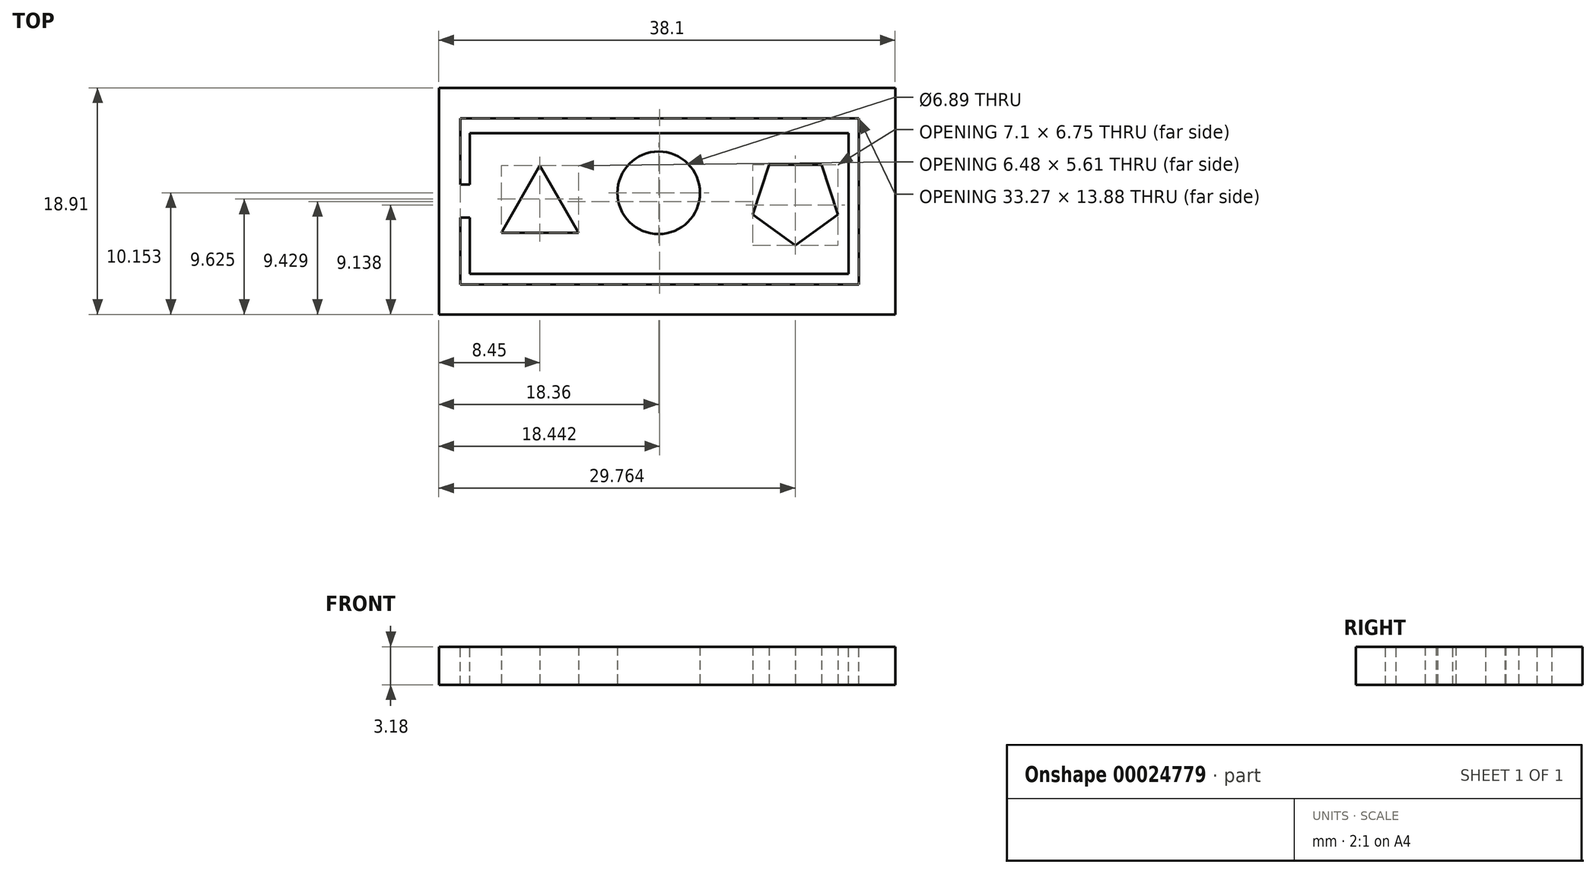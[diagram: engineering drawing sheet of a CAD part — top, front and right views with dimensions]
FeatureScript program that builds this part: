
annotation { "Feature Type Name" : "Feature", "Feature Type Description" : "" }
export const myFeature = defineFeature(function(context is Context, id is Id, definition is map)
    precondition{}
    {
        {
            var Q0;
            Q0=qCreatedBy(makeId("Top.planeOp"),FACE);
            var sketch = newSketch(context, id + "F0", { "sketchPlane" : qUnion([Q0])});
            skLineSegment(sketch, "E0", {"start": v(-18.36, 0) * mm, "end": v(19.74, 0) * mm});
            skLineSegment(sketch, "E1", {"start": v(-18.36, 0) * mm, "end": v(-18.36, 18.9) * mm});
            skLineSegment(sketch, "E2", {"start": v(-18.36, 18.9) * mm, "end": v(19.74, 18.9) * mm});
            skLineSegment(sketch, "E3", {"start": v(19.74, 18.9) * mm, "end": v(19.74, 0) * mm});
            skLineSegment(sketch, "E4", {"start": v(-9.9, 12.43) * mm, "end": v(-13.15, 6.82) * mm});
            skLineSegment(sketch, "E5", {"start": v(-13.15, 6.82) * mm, "end": v(-6.67, 6.82) * mm});
            skLineSegment(sketch, "E6", {"start": v(-6.67, 6.82) * mm, "end": v(-9.9, 12.43) * mm});
            skCircle(sketch, "E7", {"center": v(0, 10.15) * mm, "radius": 3.45 * mm});
            skCircle(sketch, "E8.cCircle", {"center": v(11.4, 9.5) * mm, "radius": 3.73 * mm, "construction": true});
            skLineSegment(sketch, "E8.0", {"start": v(11.4, 5.76) * mm, "end": v(7.86, 8.34) * mm});
            skLineSegment(sketch, "E8.1", {"start": v(7.86, 8.34) * mm, "end": v(9.21, 12.51) * mm});
            skLineSegment(sketch, "E8.2", {"start": v(9.21, 12.51) * mm, "end": v(13.6, 12.51) * mm});
            skLineSegment(sketch, "E8.3", {"start": v(13.6, 12.51) * mm, "end": v(14.95, 8.34) * mm});
            skLineSegment(sketch, "E8.4", {"start": v(14.95, 8.34) * mm, "end": v(11.4, 5.76) * mm});
            skSolve(sketch);
        }
        {
            var Q0;
            {var subQ6=sQuery(id+"F0.wireOp",EDGE,"E0");Q0=makeQuery(id+"F0.imprint","IMPRINT",FACE,{"disambiguationData":[TD([[makeQuery(id+"F0.imprint","IMPRINT",EDGE,{"derivedFrom":subQ6}),1.0]])]});}
            extrude(context, id + "F1", {"entities" : qUnion([Q0]), "depth" : 3.17 * mm});
        }
        {
            var Q0;
            Q0=makeQuery(id+"F1.opExtrude","CAP_FACE",FACE,{"disambiguationData":[OSD([sQuery(id+"F0.wireOp",EDGE,"E0"),sQuery(id+"F0.wireOp",EDGE,"E1"),sQuery(id+"F0.wireOp",EDGE,"E2"),sQuery(id+"F0.wireOp",EDGE,"E3"),sQuery(id+"F0.wireOp",EDGE,"E4"),sQuery(id+"F0.wireOp",EDGE,"E5"),sQuery(id+"F0.wireOp",EDGE,"E6"),sQuery(id+"F0.wireOp",EDGE,"E7"),sQuery(id+"F0.wireOp",EDGE,"E8.0"),sQuery(id+"F0.wireOp",EDGE,"E8.1"),sQuery(id+"F0.wireOp",EDGE,"E8.2"),sQuery(id+"F0.wireOp",EDGE,"E8.3"),sQuery(id+"F0.wireOp",EDGE,"E8.4")])],"isStart":false});
            cPlane(context, id + "F2", {"entities" : qUnion([Q0]), "cplaneType" : CPlaneType.OFFSET, "offset" : 0 * mm, "width" : 152.4 * mm, "height" : 152.4 * mm});
        }
        {
            var Q0;
            Q0=qCreatedBy(id+"F2.planeOp",FACE);
            var sketch = newSketch(context, id + "F3", { "sketchPlane" : qUnion([Q0])});
            skLineSegment(sketch, "E9", {"start": v(-16.55, 8.1) * mm, "end": v(-16.55, 2.49) * mm});
            skLineSegment(sketch, "E10", {"start": v(-16.55, 2.49) * mm, "end": v(16.72, 2.49) * mm});
            skLineSegment(sketch, "E11", {"start": v(16.72, 2.49) * mm, "end": v(16.72, 16.37) * mm});
            skLineSegment(sketch, "E12", {"start": v(16.72, 16.37) * mm, "end": v(-15.77, 16.37) * mm});
            skLineSegment(sketch, "E13", {"start": v(-16.55, 16.37) * mm, "end": v(-16.55, 10.86) * mm});
            skLineSegment(sketch, "E14.bottom", {"start": v(-16.55, 8.1) * mm, "end": v(-15.77, 8.1) * mm});
            skLineSegment(sketch, "E14.right", {"start": v(-15.77, 8.1) * mm, "end": v(-15.77, 3.38) * mm});
            skLineSegment(sketch, "E15.bottom", {"start": v(-15.77, 3.38) * mm, "end": v(15.85, 3.38) * mm});
            skLineSegment(sketch, "E16.right", {"start": v(15.85, 3.38) * mm, "end": v(15.85, 15.13) * mm});
            skLineSegment(sketch, "E17.bottom", {"start": v(15.85, 15.13) * mm, "end": v(-15.77, 15.13) * mm});
            skLineSegment(sketch, "E18.top", {"start": v(-15.77, 10.86) * mm, "end": v(-16.55, 10.86) * mm});
            skLineSegment(sketch, "E18.left", {"start": v(-15.77, 15.13) * mm, "end": v(-15.77, 10.86) * mm});
            skPoint(sketch, "E19.orphan", {"position": v(-15.77, 16.37) * mm});
            skLineSegment(sketch, "E20", {"start": v(-15.77, 16.37) * mm, "end": v(-16.55, 16.37) * mm});
            skSolve(sketch);
        }
        {
            var Q0;
            {var subQ3=sQuery(id+"F3.wireOp",EDGE,"E17.top");var subQ5=sQuery(id+"F3.wireOp",EDGE,"E16.right");var subQ6=makeQuery(id+"F3.imprint","INTERSECT",VERTEX,{"derivedFrom":[subQ5,subQ3]});Q0=makeQuery(id+"F3.imprint","IMPRINT",FACE,{"disambiguationData":[TD([[makeQuery(id+"F3.imprint","IMPRINT",EDGE,{"disambiguationData":[TD([[subQ6,1.0]])],"derivedFrom":subQ5}),1.0]])]});}
            var Q1;
            {var subQ1=sQuery(id+"F3.wireOp",EDGE,"E18.bottom");Q1=makeQuery(id+"F3.imprint","IMPRINT",FACE,{"disambiguationData":[TD([[makeQuery(id+"F3.imprint","IMPRINT",EDGE,{"derivedFrom":subQ1}),1.0]])]});}
            var Q2;
            {var subQ1=sQuery(id+"F3.wireOp",EDGE,"E18.top");Q2=makeQuery(id+"F3.imprint","IMPRINT",FACE,{"disambiguationData":[TD([[makeQuery(id+"F3.imprint","IMPRINT",EDGE,{"derivedFrom":subQ1}),-1.0]])]});}
            var Q3;
            {var subQ4=sQuery(id+"F3.wireOp",EDGE,"E14.bottom");Q3=makeQuery(id+"F3.imprint","IMPRINT",FACE,{"disambiguationData":[TD([[makeQuery(id+"F3.imprint","IMPRINT",EDGE,{"derivedFrom":subQ4}),-1.0]])]});}
            var Q4;
            {var subQ0=sQuery(id+"F3.wireOp",EDGE,"E15.left");Q4=makeQuery(id+"F3.imprint","IMPRINT",FACE,{"disambiguationData":[TD([[makeQuery(id+"F3.imprint","IMPRINT",EDGE,{"derivedFrom":subQ0}),1.0]])]});}
            var Q5;
            {var subQ3=sQuery(id+"F3.wireOp",EDGE,"E15.top");var subQ5=sQuery(id+"F3.wireOp",EDGE,"E14.right");var subQ7=makeQuery(id+"F3.imprint","INTERSECT",VERTEX,{"derivedFrom":[subQ5,subQ3]});Q5=makeQuery(id+"F3.imprint","IMPRINT",FACE,{"disambiguationData":[TD([[makeQuery(id+"F3.imprint","IMPRINT",EDGE,{"disambiguationData":[TD([[subQ7,1.0]])],"derivedFrom":subQ5}),1.0]])]});}
            var Q6;
            {var subQ3=sQuery(id+"F3.wireOp",EDGE,"E16.bottom");Q6=makeQuery(id+"F3.imprint","IMPRINT",FACE,{"disambiguationData":[TD([[makeQuery(id+"F3.imprint","IMPRINT",EDGE,{"derivedFrom":subQ3}),-1.0]])]});}
            var Q7;
            {var subQ3=sQuery(id+"F3.wireOp",EDGE,"E16.left");var subQ5=sQuery(id+"F3.wireOp",EDGE,"E15.bottom");var subQ7=makeQuery(id+"F3.imprint","INTERSECT",VERTEX,{"derivedFrom":[subQ5,subQ3]});Q7=makeQuery(id+"F3.imprint","IMPRINT",FACE,{"disambiguationData":[TD([[makeQuery(id+"F3.imprint","IMPRINT",EDGE,{"disambiguationData":[TD([[subQ7,1.0]])],"derivedFrom":subQ5}),1.0]])]});}
            var Q8;
            {var subQ0=sQuery(id+"F3.wireOp",EDGE,"E17.left");Q8=makeQuery(id+"F3.imprint","IMPRINT",FACE,{"disambiguationData":[TD([[makeQuery(id+"F3.imprint","IMPRINT",EDGE,{"derivedFrom":subQ0}),1.0]])]});}
            extrude(context, id + "F4", {"entities" : qUnion([Q0, Q1, Q2, Q3, Q4, Q5, Q6, Q7, Q8]), "operationType" : NewBodyOperationType.REMOVE, "oppositeDirection" : true, "depth" : 25.4 * mm});
        }
    });
